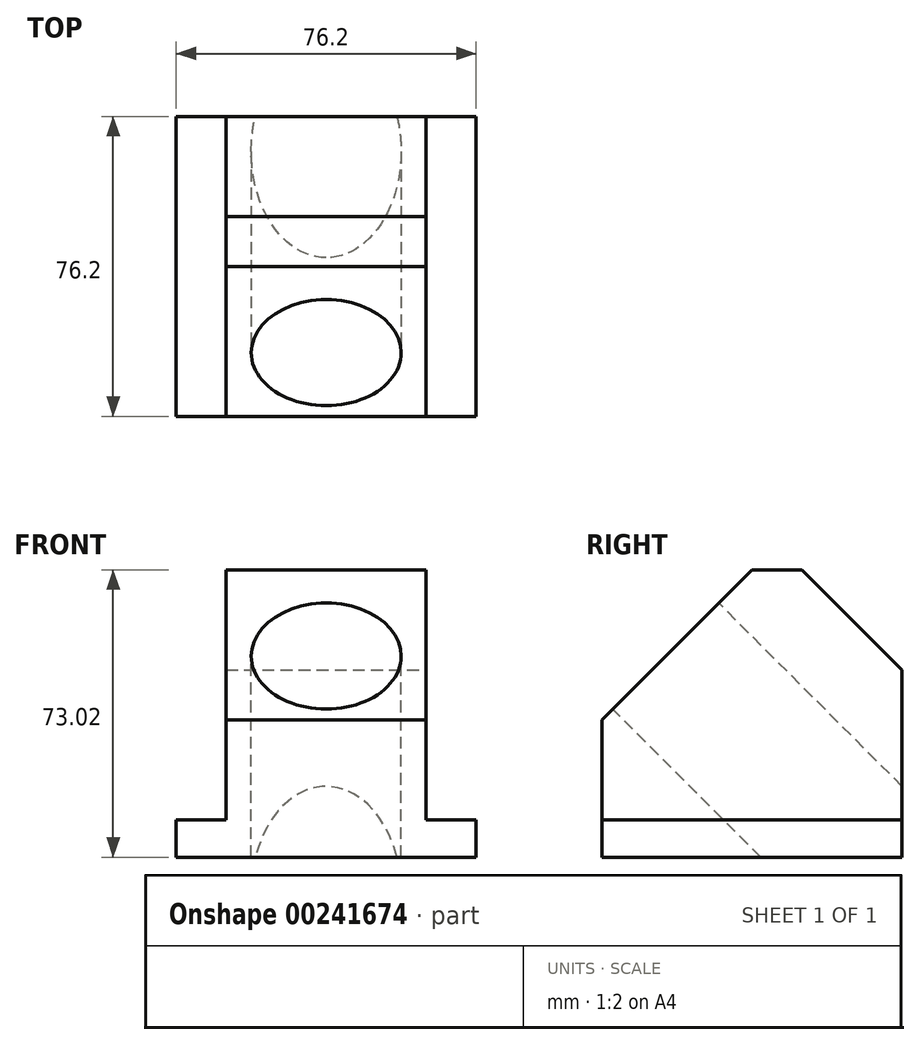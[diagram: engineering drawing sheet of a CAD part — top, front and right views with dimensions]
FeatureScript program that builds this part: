
annotation { "Feature Type Name" : "Feature", "Feature Type Description" : "" }
export const myFeature = defineFeature(function(context is Context, id is Id, definition is map)
    precondition{}
    {
        {
            var Q0;
            Q0=qCreatedBy(makeId("Front.planeOp"),FACE);
            var sketch = newSketch(context, id + "F0", { "sketchPlane" : qUnion([Q0])});
            skLineSegment(sketch, "E0.bottom", {"start": v(38.1, 4.76) * mm, "end": v(-38.1, 4.76) * mm});
            skLineSegment(sketch, "E0.top", {"start": v(38.1, -4.76) * mm, "end": v(-38.1, -4.76) * mm});
            skLineSegment(sketch, "E0.left", {"start": v(38.1, 4.76) * mm, "end": v(38.1, -4.76) * mm});
            skLineSegment(sketch, "E0.right", {"start": v(-38.1, 4.76) * mm, "end": v(-38.1, -4.76) * mm});
            skPoint(sketch, "E0.middle", {"position": v(0, 0) * mm});
            skSolve(sketch);
        }
        {
            var Q0;
            Q0 = qSketchRegion(id + "F0", true);
            extrude(context, id + "F1", {"entities" : qUnion([Q0]), "endBound" : BoundingType.SYMMETRIC, "depth" : 76.2 * mm});
        }
        {
            var Q0;
            Q0=makeQuery(id+"F1.opExtrude","SWEPT_FACE",FACE,{"disambiguationData":[OSD([sQuery(id+"F0.wireOp",EDGE,"E0.bottom")])]});
            var sketch = newSketch(context, id + "F2", { "sketchPlane" : qUnion([Q0])});
            skLineSegment(sketch, "E1.bottom", {"start": v(25.4, 38.1) * mm, "end": v(-25.4, 38.1) * mm});
            skLineSegment(sketch, "E1.top", {"start": v(25.4, -38.1) * mm, "end": v(-25.4, -38.1) * mm});
            skLineSegment(sketch, "E1.left", {"start": v(25.4, 38.1) * mm, "end": v(25.4, -38.1) * mm});
            skLineSegment(sketch, "E1.right", {"start": v(-25.4, 38.1) * mm, "end": v(-25.4, -38.1) * mm});
            skPoint(sketch, "E1.middle", {"position": v(0, 0) * mm});
            skSolve(sketch);
        }
        {
            var Q0;
            Q0 = qSketchRegion(id + "F2", true);
            extrude(context, id + "F3", {"entities" : qUnion([Q0]), "operationType" : NewBodyOperationType.ADD, "depth" : 63.5 * mm});
        }
        {
            var Q0;
            Q0=makeQuery(id+"F3.opExtrude","CAP_EDGE",EDGE,{"disambiguationData":[OSD([sQuery(id+"F2.wireOp",EDGE,"E1.top")])],"isStart":false});
            chamfer(context, id + "F4", {"entities" : qUnion([Q0]), "chamferType" : ChamferType.OFFSET_ANGLE, "width" : 38.1 * mm, "oppositeDirection" : false, "angle" : 45 * degree, "tangentPropagation" : true});
        }
        {
            var Q0;
            Q0=makeQuery(id+"F4.opChamfer","BLEND_FACE",FACE,{"disambiguationData":[OSD([sQuery(id+"F2.wireOp",EDGE,"E1.top")])]});
            var sketch = newSketch(context, id + "F5", { "sketchPlane" : qUnion([Q0])});
            skCircle(sketch, "E2", {"center": v(0, 17.25) * mm, "radius": 19.05 * mm});
            skSolve(sketch);
        }
        {
            var Q0;
            Q0 = qSketchRegion(id + "F5", true);
            extrude(context, id + "F6", {"entities" : qUnion([Q0]), "operationType" : NewBodyOperationType.REMOVE, "oppositeDirection" : true, "depth" : 190.25 * mm});
        }
        {
            var Q0;
            Q0=makeQuery(id+"F3.opExtrude","CAP_EDGE",EDGE,{"disambiguationData":[OSD([sQuery(id+"F2.wireOp",EDGE,"E1.bottom")])],"isStart":false});
            chamfer(context, id + "F7", {"entities" : qUnion([Q0]), "width" : 25.4 * mm, "tangentPropagation" : true});
        }
    });
